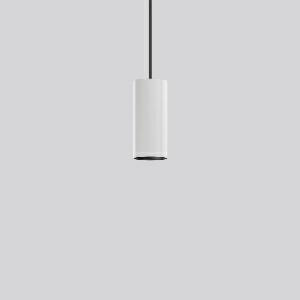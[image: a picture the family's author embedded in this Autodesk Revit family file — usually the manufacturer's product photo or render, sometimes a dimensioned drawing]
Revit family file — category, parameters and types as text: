
# Revit family: deecos_p_mini_911522_002_1_dcd2
name_source: partatom
category: Lighting Fixtures
units: mm (PartAtom-declared; Revit-internal decimal feet)

## family parameters
Cut with Voids When Loaded = No
Host = Face
Light Source = No
Part Type = Normal
Room Calculation Point = No
Round Connector Dimension = Use Diameter
Shared = No

## types (1)
- DEECOS P mini (1 x LED Modul 940, 3700 lm, 4000)
    Apparent Load = 29 VA
    Approval mark = CE
    CIE Flux Codes = 99 100 100 100 100
    Color Rendering = 92
    Color Temperature = 4000
    Default Elevation = 1800 mm
    Description = Series: DEECOS P mini
Cylindrical pendant luminaire. Housing: die-cast aluminium, powder-coated. Canopy made of powder-coated sheet steel with magnetic attachment. Optical assembly with reflector made of MIRO-Silver with 98% total light reflection for outstanding efficiency - can be changed without tools. Best colour rendering index Ra>90. Transparent pendant cable 5 m, can be shortened, with integrated steel cable. High quality converter without flickering and stroboscopic effect. The following accessories can be mounted without use of tools: interchangeable lenses, honeycomb louvre, clear and frosted diffusers, white interchangeable plastic ring. Decorative recessed suspension set available as accessory.Suitable for accessory Deecos P Tube cylinder extensions 0.5 m, 0.75 m or 1 m. 
Colour: traffic white, matt (RAL 9016)
Diameter: 87 mm
Height: 195 mm
Suspension length: 5000 mm
Lamp: LED
Socket: without socket
Colour temperature: 4000K
Colour rendering index (CRI): 92
System power: 29 W
Rated luminous flux: 3700 lm
Luminous efficiency: 128 lm/W
Control gear: Regulated power supply
Protection class: I
Type of protection: IP 20
    Height = 195 mm
    Lamp = 1 x LED Modul 940
    Lamp Light Flux = 3700 lm
    Lamp count = 1
    Length = 87 mm
    Lifetime = 50000 h
    Luminous efficacy = 128 lm/W
    Manufacturer = RZB
    ModVariant = No
    Model = 911522.002.1
    Mounting Place = Ceiling
    Mounting Type = Pendant
    Number of Poles = 1
    OnlyDefault = Yes
    Power Factor = 1
    Product Name = DEECOS P mini
    Product group = Pendant luminaires
    ProductGroupID = 902
    Protection Class = Protection class I
    Protection Degree = IP 20
    RLX_Detail_Level = 1
    RLX_Emergency_Light_Flux = 0 lm
    RLX_Emergency_Type = 0
    RLX_Emergency_Type_DB = No
    RlxData = <blob elided: 55005 chars, md5=78ef17fb>
    Socket = socket
    Standby Power = 0 W
    System Light Flux = 3700 lm
    System Power = 29 W
    Type Comments = Product without accessories
    Type Image = 911476.002.jpg
    URL = http://relux.com
    VarID = ---
    Voltage = 230 V
    Voltage Range = 220-240 V
    Weight = 0.00 kg
    Width = 0 mm  [stored 0 ft]

note: [stored X ft] marks values corroborated as IEEE doubles in the binary element streams (Revit-internal decimal feet)

## geometry (parser evidence)
native form markers: Blend x4, Sweep x13
no freeform markers — native parametric forms only
